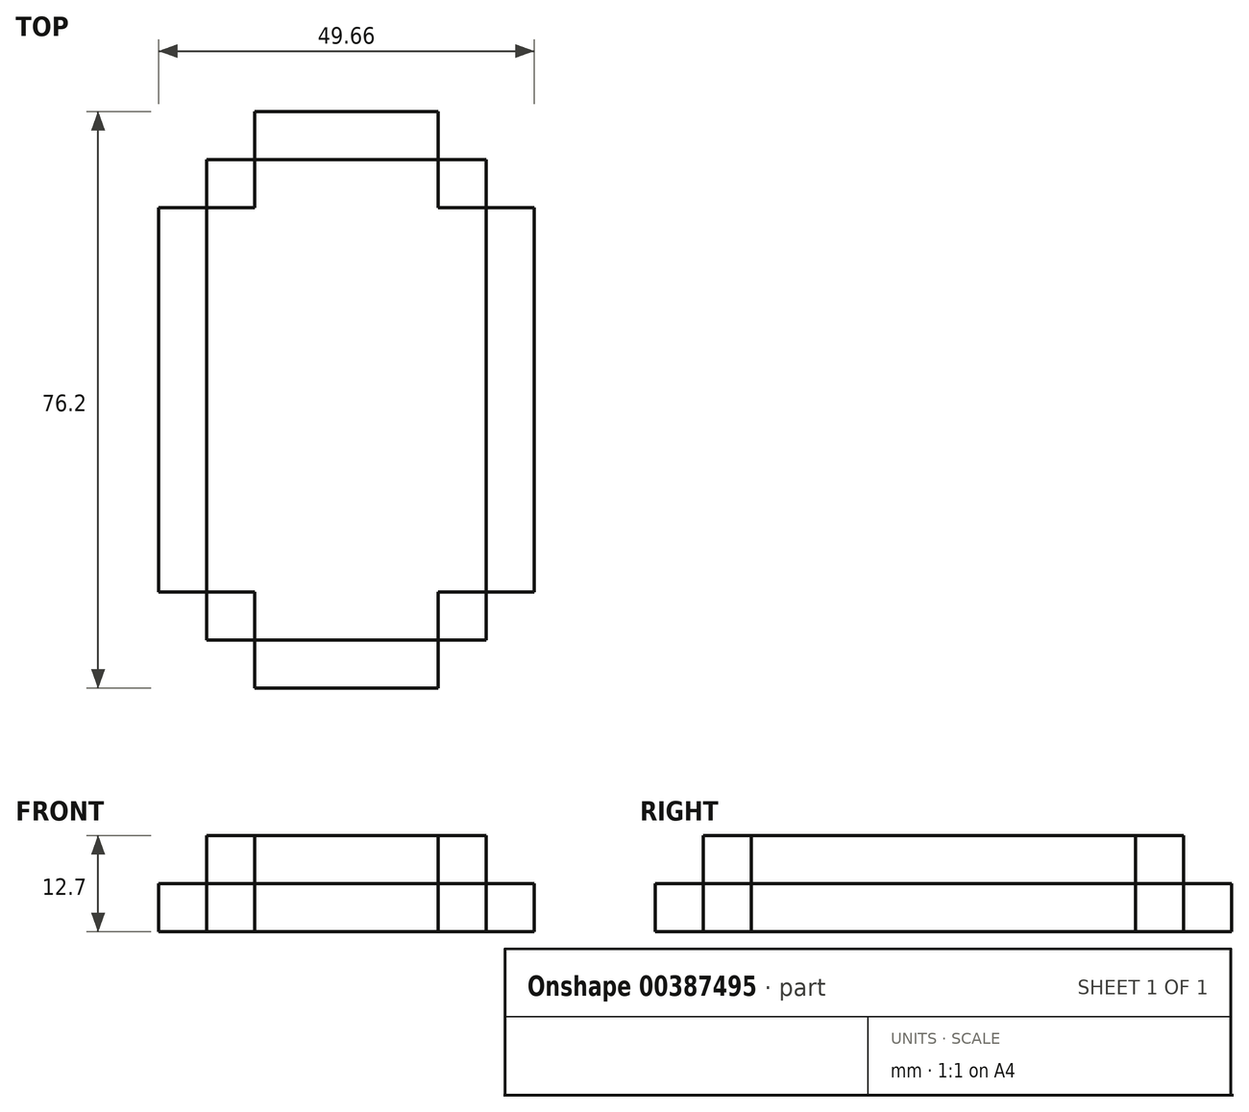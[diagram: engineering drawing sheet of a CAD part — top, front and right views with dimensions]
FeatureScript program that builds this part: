
annotation { "Feature Type Name" : "Feature", "Feature Type Description" : "" }
export const myFeature = defineFeature(function(context is Context, id is Id, definition is map)
    precondition{}
    {
        {
            var Q0;
            Q0=qCreatedBy(makeId("Top.planeOp"),FACE);
            var sketch = newSketch(context, id + "F0", { "sketchPlane" : qUnion([Q0])});
            skLineSegment(sketch, "E0.bottom", {"start": v(-13.18, 37.27) * mm, "end": v(11.08, 37.27) * mm});
            skLineSegment(sketch, "E0.top", {"start": v(-13.18, -38.93) * mm, "end": v(11.08, -38.93) * mm});
            skLineSegment(sketch, "E0.left", {"start": v(-25.88, 24.57) * mm, "end": v(-25.88, -26.23) * mm});
            skLineSegment(sketch, "E0.right", {"start": v(23.78, 24.57) * mm, "end": v(23.78, -26.23) * mm});
            skLineSegment(sketch, "E1", {"start": v(-25.88, 24.57) * mm, "end": v(-19.53, 24.57) * mm});
            skLineSegment(sketch, "E2", {"start": v(-19.53, 24.57) * mm, "end": v(-19.53, 30.92) * mm});
            skLineSegment(sketch, "E3", {"start": v(-19.53, 30.92) * mm, "end": v(-13.18, 30.92) * mm});
            skLineSegment(sketch, "E4", {"start": v(-13.18, 30.92) * mm, "end": v(-13.18, 37.27) * mm});
            skPoint(sketch, "E5.orphan", {"position": v(-25.88, 37.27) * mm});
            skLineSegment(sketch, "E6", {"start": v(11.08, 37.27) * mm, "end": v(11.08, 30.92) * mm});
            skLineSegment(sketch, "E7", {"start": v(11.08, 30.92) * mm, "end": v(17.43, 30.92) * mm});
            skLineSegment(sketch, "E8", {"start": v(17.43, 30.92) * mm, "end": v(17.43, 24.57) * mm});
            skLineSegment(sketch, "E9", {"start": v(17.43, 24.57) * mm, "end": v(23.78, 24.57) * mm});
            skLineSegment(sketch, "E10", {"start": v(23.78, -26.23) * mm, "end": v(17.43, -26.23) * mm});
            skLineSegment(sketch, "E11", {"start": v(17.43, -26.23) * mm, "end": v(17.43, -32.58) * mm});
            skLineSegment(sketch, "E12", {"start": v(17.43, -32.58) * mm, "end": v(11.08, -32.58) * mm});
            skLineSegment(sketch, "E13", {"start": v(11.08, -32.58) * mm, "end": v(11.08, -38.93) * mm});
            skLineSegment(sketch, "E14", {"start": v(-25.88, -26.23) * mm, "end": v(-19.53, -26.23) * mm});
            skLineSegment(sketch, "E15", {"start": v(-19.53, -26.23) * mm, "end": v(-19.53, -32.58) * mm});
            skLineSegment(sketch, "E16", {"start": v(-19.53, -32.58) * mm, "end": v(-13.18, -32.58) * mm});
            skLineSegment(sketch, "E17", {"start": v(-13.18, -32.58) * mm, "end": v(-13.18, -38.93) * mm});
            skSolve(sketch);
        }
        {
            var Q0;
            Q0 = qSketchRegion(id + "F0", true);
            extrude(context, id + "F1", {"entities" : qUnion([Q0]), "depth" : 6.35 * mm});
        }
        {
            var Q0;
            Q0=makeQuery(id+"F1.opExtrude","CAP_FACE",FACE,{"disambiguationData":[OSD([sQuery(id+"F0.wireOp",EDGE,"E0.bottom"),sQuery(id+"F0.wireOp",EDGE,"E0.top"),sQuery(id+"F0.wireOp",EDGE,"E0.left"),sQuery(id+"F0.wireOp",EDGE,"E0.right"),sQuery(id+"F0.wireOp",EDGE,"E1"),sQuery(id+"F0.wireOp",EDGE,"E2"),sQuery(id+"F0.wireOp",EDGE,"E3"),sQuery(id+"F0.wireOp",EDGE,"E4"),sQuery(id+"F0.wireOp",EDGE,"E6"),sQuery(id+"F0.wireOp",EDGE,"E7"),sQuery(id+"F0.wireOp",EDGE,"E8"),sQuery(id+"F0.wireOp",EDGE,"E9"),sQuery(id+"F0.wireOp",EDGE,"E10"),sQuery(id+"F0.wireOp",EDGE,"E11"),sQuery(id+"F0.wireOp",EDGE,"E12"),sQuery(id+"F0.wireOp",EDGE,"E13"),sQuery(id+"F0.wireOp",EDGE,"E14"),sQuery(id+"F0.wireOp",EDGE,"E15"),sQuery(id+"F0.wireOp",EDGE,"E16"),sQuery(id+"F0.wireOp",EDGE,"E17")])],"isStart":false});
            var sketch = newSketch(context, id + "F2", { "sketchPlane" : qUnion([Q0])});
            skLineSegment(sketch, "E18.bottom", {"start": v(-13.18, 30.92) * mm, "end": v(11.08, 30.92) * mm});
            skLineSegment(sketch, "E18.top", {"start": v(-13.18, -32.58) * mm, "end": v(11.08, -32.58) * mm});
            skLineSegment(sketch, "E18.left", {"start": v(-19.53, 24.57) * mm, "end": v(-19.53, -26.23) * mm});
            skLineSegment(sketch, "E18.right", {"start": v(17.43, 24.57) * mm, "end": v(17.43, -26.23) * mm});
            skLineSegment(sketch, "E19", {"start": v(-13.18, 30.92) * mm, "end": v(-13.18, 24.57) * mm});
            skLineSegment(sketch, "E20", {"start": v(-13.18, 24.57) * mm, "end": v(-19.53, 24.57) * mm});
            skLineSegment(sketch, "E21", {"start": v(11.08, 30.92) * mm, "end": v(11.08, 24.57) * mm});
            skLineSegment(sketch, "E22", {"start": v(11.08, 24.57) * mm, "end": v(17.43, 24.57) * mm});
            skLineSegment(sketch, "E23", {"start": v(-19.53, -26.23) * mm, "end": v(-13.18, -26.23) * mm});
            skLineSegment(sketch, "E24", {"start": v(-13.18, -26.23) * mm, "end": v(-13.18, -32.58) * mm});
            skLineSegment(sketch, "E25", {"start": v(11.08, -32.58) * mm, "end": v(11.08, -26.23) * mm});
            skLineSegment(sketch, "E26", {"start": v(11.08, -26.23) * mm, "end": v(17.43, -26.23) * mm});
            skSolve(sketch);
        }
        {
            var Q0;
            Q0 = qSketchRegion(id + "F2", true);
            extrude(context, id + "F3", {"entities" : qUnion([Q0]), "operationType" : NewBodyOperationType.ADD, "depth" : 6.35 * mm});
        }
    });
